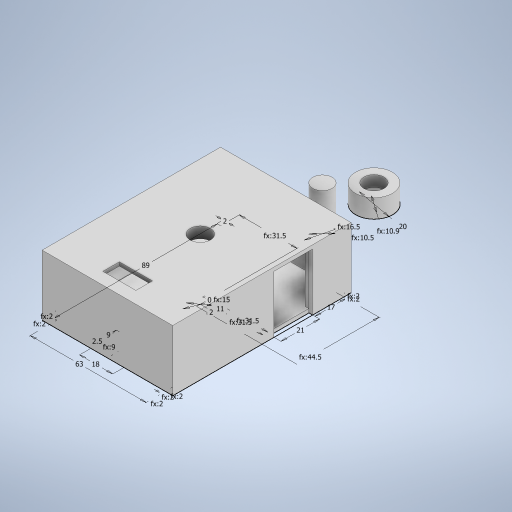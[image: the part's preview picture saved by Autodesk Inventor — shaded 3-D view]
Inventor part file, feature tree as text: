
AUTODESK INVENTOR PART (.ipt)
format: ipt  version: 2024 (Build 280153000, 153)  size: 365,056 bytes
history: native  units: mm
features: extrude x15, other x4
ambient origin geometry x8: Origin, YZ Plane, XZ Plane, XY Plane, X Axis, Y Axis, Z Axis, Center Point
bodies: Body1 (feature_tree), Body2 (feature_tree), Body3 (feature_tree)
feature tree (19):
  other  "Inside"
  other  "Bottom_sketch"
  extrude  "Bottom"  Depth=31.5mm
  extrude  "Side_Inside"  Depth=44.5mm
  extrude  "Side_Outside"  Depth=2.0mm
  extrude  "Top"  Depth=2.0mm
  extrude  "Lora_Hole"  Depth=2.0mm
  extrude  "TTL_Hole"  Depth=2.0mm TaperAngle=0.0deg
  extrude  "TTL_Outside"  TaperAngle=0.0deg  [1 undecoded]
  extrude  "Button_Hole"  Depth=2.0mm
  extrude  "Lora_Outside"  Depth=2.0mm
  extrude  "Button_slide"  Depth=2.0mm
  extrude  "TTL_Hole_v2"  Depth=2.0mm
  extrude  "Button_Piece"  Depth=31.0mm TaperAngle=0.0deg
  extrude  "Button_Bottom"  Depth=2.0mm TaperAngle=0.0deg
  extrude  "Button_Mushroom"  Depth=17.0mm
  extrude  "Mushroom_Inside"  Depth=29.0mm
  other  "Outside"
  other  "Button"
note: 1 required parameter value undecoded (feature->parameter linkage not recoverable at this tier; creation-order binding heuristic only, values carry confidence <= 0.55)
